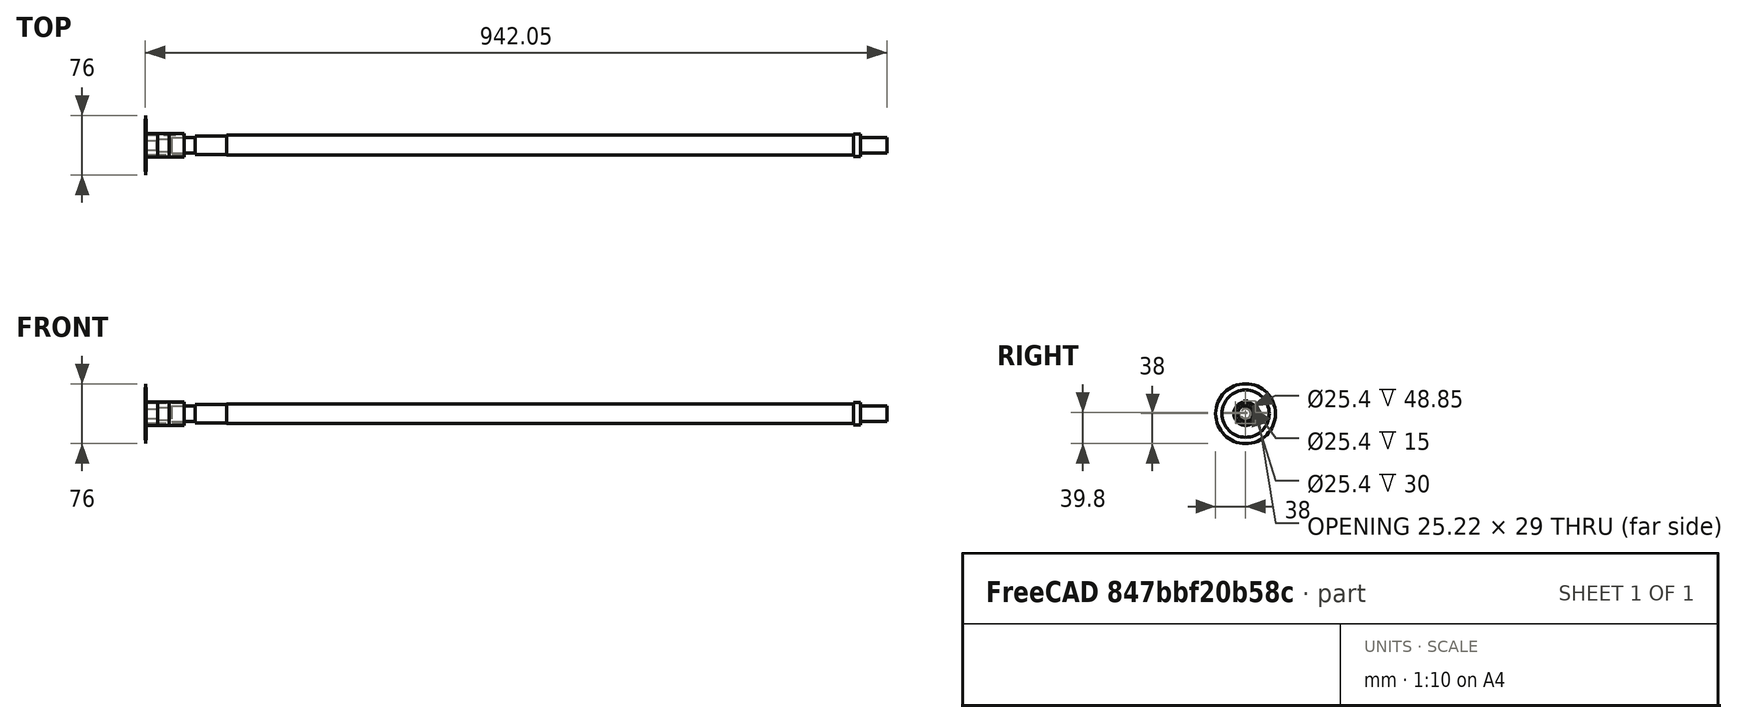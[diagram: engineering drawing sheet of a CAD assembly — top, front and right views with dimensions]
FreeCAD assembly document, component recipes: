
FREECAD ASSEMBLY — COMPONENT RECIPES ("cutting_roll")

This assembly document has 5 components, labeled P0..P4 below (a component is one placed body or linked part). 5 of them carry a construction recipe — the FreeCAD feature program that regenerates the part from scratch, quoted from this document or its linked companion documents; the rest are supplied as boundary geometry only. No exploded tour is included for this assembly.
COMPONENT P0 — recipe-attached ("spacer_49mm", modeled in this document).
Construction recipe (the document's own serialized feature program — sketch geometry with constraints, then the solid features built on it; lengths are millimeters unless a unit is written):

FEATURE [Sketcher::SketchObject] Sketch
  FullyConstrained = true
  MapMode = 5
  Placement = pos=(0,0,0) rot=(0.57735,0.57735,0.57735;2.0944rad)
  Support = -> [YZ_Plane]
  sketch-geometry (2):
    g0: Circle CenterX=0 CenterY=0 CenterZ=0 NormalX=0 NormalY=0 NormalZ=1 AngleXU=0 Radius=14.85
    g1: Circle CenterX=0 CenterY=0 CenterZ=0 NormalX=0 NormalY=0 NormalZ=1 AngleXU=0 Radius=12.7
  constraints (4):
    c: Coincident(g0,g-1)
    c: Diameter(g0) = 29.7  'outer_d'
    c: Coincident(g1,g0)
    c: Diameter(g1) = 25.4  'inner_d'
FEATURE [PartDesign::Pad] Pad  label="spacer_49_pad"
  Direction = (1,-2e-16,3e-16)
  Length = 48.85
  Length2 = 10
  Placement = pos=(0,0,0) rot=(0.57735,0.57735,0.57735;2.0944rad)
  Profile = -> Sketch
  ReferenceAxis = -> Sketch [N_Axis]
  Type = 0
FEATURE [PartDesign::CoordinateSystem] front
  AttacherType = Attacher::AttachEngine3D
  MapMode = 5
  Support = -> [XY_Plane]
FEATURE [PartDesign::CoordinateSystem] back
  AttacherType = Attacher::AttachEngine3D
  AttachmentOffset = pos=(48.85,0,0) rot=(0,0,1;0rad)
  MapMode = 5
  Placement = pos=(48.85,0,0) rot=(0,0,1;0rad)
  Support = -> [XY_Plane]
  expr: .AttachmentOffset.Base.x = Pad.Length
FEATURE [PartDesign::Body] Body  label="spacer_49mm"
  Group = -> [Sketch,Pad,front,back]
  Origin = -> Origin
  Tip = -> Pad
COMPONENT P1 — recipe-attached ("cutting_disk", modeled in this document).
Construction recipe (the document's own serialized feature program — sketch geometry with constraints, then the solid features built on it; lengths are millimeters unless a unit is written):

FEATURE [Sketcher::SketchObject] Sketch001  label="disk_sketch"
  FullyConstrained = true
  MapMode = 5
  Placement = pos=(0,0,0) rot=(1,0,0;1.5708rad)
  Support = -> [XZ_Plane001]
  sketch-geometry (4):
    g0: LineSegment StartX=0 StartY=38 StartZ=0 EndX=0.55 EndY=30 EndZ=0
    g1: LineSegment StartX=0.55 StartY=30 StartZ=0 EndX=0.55 EndY=0 EndZ=0
    g2: LineSegment StartX=0.55 StartY=0 StartZ=0 EndX=0 EndY=0 EndZ=0
    g3: LineSegment StartX=0 StartY=0 StartZ=0 EndX=0 EndY=38 EndZ=0
  constraints (11):
    c: PointOnObject(g0,g-2)
    c: Coincident(g1,g0)
    c: Vertical(g1)
    c: Coincident(g2,g1)
    c: Horizontal(g2)
    c: Coincident(g3,g2)
    c: Coincident(g3,g0)
    c: Coincident(g2,g-1)
    c: Distance(g3) = 38  'r'
    c: Distance(g2) = 0.55  'thickness_x2'
    c: Distance(g1) = 30
FEATURE [PartDesign::Revolution] Revolution
  Angle = 360
  Axis = (1,0,0)
  Base = (0,0,0)
  Placement = pos=(0,0,0) rot=(1,0,0;1.5708rad)
  Profile = -> Sketch001
  ReferenceAxis = -> Sketch001 [H_Axis]
FEATURE [Sketcher::SketchObject] Sketch002
  FullyConstrained = true
  MapMode = 5
  Placement = pos=(0,0,0) rot=(0.57735,0.57735,0.57735;2.0944rad)
  Support = -> [YZ_Plane001]
  sketch-geometry (4):
    g0: LineSegment StartX=3 StartY=12.3406 StartZ=0 EndX=3 EndY=16.3 EndZ=0
    g1: LineSegment StartX=3 StartY=16.3 StartZ=0 EndX=0 EndY=16.3 EndZ=0
    g2: LineSegment StartX=0 StartY=16.3 StartZ=0 EndX=0 EndY=-12.7 EndZ=0
    g3: ArcOfCircle CenterX=0 CenterY=0 CenterZ=0 NormalX=0 NormalY=0 NormalZ=1 AngleXU=0 Radius=12.7 StartAngle=4.71239 EndAngle=7.61551
  constraints (12):
    c: Vertical(g0)
    c: Coincident(g0,g1)
    c: PointOnObject(g1,g-2)
    c: Horizontal(g1)
    c: Coincident(g1,g2)
    c: PointOnObject(g2,g-2)
    c: Coincident(g3,g-1)
    c: Coincident(g3,g2)
    c: Coincident(g3,g0)
    c: Diameter(g3) = 25.4
    c: Distance(g1) = 3
    c: Distance(g2) = 29
FEATURE [PartDesign::Mirrored] Mirrored
  BaseFeature = -> Revolution
  MirrorPlane = -> Sketch001 [V_Axis]
  Originals = -> [Revolution]
  Placement = pos=(0,0,0) rot=(1,0,0;1.5708rad)
FEATURE [PartDesign::Pocket] Pocket
  BaseFeature = -> Mirrored
  Direction = (-1,2e-16,-3e-16)
  Length = 5
  Length2 = 5
  Midplane = true
  Placement = pos=(0,0,0) rot=(1,0,0;1.5708rad)
  Profile = -> Sketch002
  ReferenceAxis = -> Sketch002 [N_Axis]
  Type = 1
FEATURE [PartDesign::Mirrored] Mirrored001
  BaseFeature = -> Pocket
  MirrorPlane = -> Sketch002 [V_Axis]
  Originals = -> [Pocket]
  Placement = pos=(0,0,0) rot=(1,0,0;1.5708rad)
FEATURE [PartDesign::CoordinateSystem] Local_CS002  label="disk_end"
  AttacherType = Attacher::AttachEngine3D
  AttachmentOffset = pos=(0.55,0,0) rot=(0,0,1;0rad)
  MapMode = 5
  Placement = pos=(0.55,0,0) rot=(0,0,1;0rad)
  Support = -> [XY_Plane001]
  expr: .AttachmentOffset.Base.x = Sketch001.Constraints.thickness_x2
FEATURE [PartDesign::CoordinateSystem] Local_CS003  label="disk_begin"
  AttacherType = Attacher::AttachEngine3D
  AttachmentOffset = pos=(-0.55,0,0) rot=(0,0,1;0rad)
  MapMode = 5
  Placement = pos=(-0.55,0,0) rot=(0,0,1;0rad)
  Support = -> [XY_Plane001]
  expr: .AttachmentOffset.Base.x = -Sketch001.Constraints.thickness_x2
FEATURE [PartDesign::CoordinateSystem] Local_CS006  label="disk_middle"
  AttacherType = Attacher::AttachEngine3D
  MapMode = 5
  Support = -> [XY_Plane001]
FEATURE [PartDesign::Body] Body001  label="cutting_disk"
  Group = -> [Sketch001,Revolution,Sketch002,Mirrored,Pocket,Mirrored001,Local_CS002,Local_CS003,Local_CS006]
  Origin = -> Origin001
  Tip = -> Mirrored001
COMPONENT P2 — recipe-attached ("spacer_15mm", modeled in this document).
Construction recipe (the document's own serialized feature program — sketch geometry with constraints, then the solid features built on it; lengths are millimeters unless a unit is written):

FEATURE [Sketcher::SketchObject] Sketch003
  FullyConstrained = true
  MapMode = 5
  Placement = pos=(0,0,0) rot=(0.57735,0.57735,0.57735;2.0944rad)
  Support = -> [YZ_Plane004]
  sketch-geometry (2):
    g0: Circle CenterX=0 CenterY=0 CenterZ=0 NormalX=0 NormalY=0 NormalZ=1 AngleXU=0 Radius=14.85
    g1: Circle CenterX=0 CenterY=0 CenterZ=0 NormalX=0 NormalY=0 NormalZ=1 AngleXU=0 Radius=12.7
  constraints (4):
    c: Coincident(g0,g-1)
    c: Diameter(g0) = 29.7
    c: Coincident(g1,g0)
    c: Diameter(g1) = 25.4
FEATURE [PartDesign::Pad] Pad001
  Direction = (1,-2e-16,3e-16)
  Length = 15
  Length2 = 10
  Placement = pos=(0,0,0) rot=(0.57735,0.57735,0.57735;2.0944rad)
  Profile = -> Sketch003
  ReferenceAxis = -> Sketch003 [N_Axis]
  Type = 0
FEATURE [PartDesign::CoordinateSystem] back001
  AttacherType = Attacher::AttachEngine3D
  AttachmentOffset = pos=(15,0,0) rot=(0,0,1;0rad)
  MapMode = 5
  Placement = pos=(15,0,0) rot=(0,0,1;0rad)
  Support = -> [XY_Plane004]
  expr: .AttachmentOffset.Base.x = Pad001.Length
FEATURE [PartDesign::CoordinateSystem] front001
  AttacherType = Attacher::AttachEngine3D
  MapMode = 5
  Support = -> [XY_Plane004]
FEATURE [PartDesign::Body] Body002  label="spacer_15mm"
  Group = -> [Sketch003,Pad001,front001,back001]
  Origin = -> Origin004
  Tip = -> Pad001
COMPONENT P3 — recipe-attached ("spacer_30mm", modeled in this document).
Construction recipe (the document's own serialized feature program — sketch geometry with constraints, then the solid features built on it; lengths are millimeters unless a unit is written):

FEATURE [Sketcher::SketchObject] Sketch004
  FullyConstrained = true
  MapMode = 5
  Placement = pos=(0,0,0) rot=(0.57735,0.57735,0.57735;2.0944rad)
  Support = -> [YZ_Plane005]
  sketch-geometry (2):
    g0: Circle CenterX=0 CenterY=0 CenterZ=0 NormalX=0 NormalY=0 NormalZ=1 AngleXU=0 Radius=14.85
    g1: Circle CenterX=0 CenterY=0 CenterZ=0 NormalX=0 NormalY=0 NormalZ=1 AngleXU=0 Radius=12.7
  constraints (4):
    c: Coincident(g0,g-1)
    c: Diameter(g0) = 29.7
    c: Coincident(g1,g0)
    c: Diameter(g1) = 25.4
FEATURE [PartDesign::Pad] Pad002
  Direction = (1,-2e-16,3e-16)
  Length = 30
  Length2 = 10
  Placement = pos=(0,0,0) rot=(0.57735,0.57735,0.57735;2.0944rad)
  Profile = -> Sketch004
  ReferenceAxis = -> Sketch004 [N_Axis]
  Type = 0
FEATURE [PartDesign::CoordinateSystem] back002
  AttacherType = Attacher::AttachEngine3D
  AttachmentOffset = pos=(30,0,0) rot=(0,0,1;0rad)
  MapMode = 5
  Placement = pos=(30,0,0) rot=(0,0,1;0rad)
  Support = -> [XY_Plane005]
  expr: .AttachmentOffset.Base.x = Pad002.Length
FEATURE [PartDesign::CoordinateSystem] front002
  AttacherType = Attacher::AttachEngine3D
  MapMode = 5
  Support = -> [XY_Plane005]
FEATURE [PartDesign::Body] Body003  label="spacer_30mm"
  Group = -> [Sketch004,Pad002,front002,back002]
  Origin = -> Origin005
  Tip = -> Pad002
COMPONENT P4 — recipe-attached ("axis", modeled in this document).
Construction recipe (the document's own serialized feature program — sketch geometry with constraints, then the solid features built on it; lengths are millimeters unless a unit is written):

FEATURE [PartDesign::CoordinateSystem] LCS_0
  AttacherType = Attacher::AttachEngine3D
  MapMode = 2
  Support = -> [X_Axis006]
FEATURE [Sketcher::SketchObject] Sketch006
  FullyConstrained = true
  MapMode = 5
  Placement = pos=(0,0,0) rot=(1,0,0;1.5708rad)
  Support = -> [XZ_Plane006]
  sketch-geometry (18):
    g0: LineSegment StartX=0 StartY=0 StartZ=0 EndX=0 EndY=6 EndZ=0
    g1: LineSegment StartX=0 StartY=6 StartZ=0 EndX=14 EndY=6 EndZ=0
    g2: LineSegment StartX=16 StartY=6.25 StartZ=0 EndX=16 EndY=8 EndZ=0
    g3: LineSegment StartX=16 StartY=8 StartZ=0 EndX=33 EndY=8 EndZ=0
    g4: LineSegment StartX=33 StartY=8 StartZ=0 EndX=33 EndY=10 EndZ=0
    g5: LineSegment StartX=33 StartY=10 StartZ=0 EndX=63 EndY=10 EndZ=0
    g6: LineSegment StartX=63 StartY=10 StartZ=0 EndX=63 EndY=12 EndZ=0
    g7: LineSegment StartX=63 StartY=12 StartZ=0 EndX=103 EndY=12 EndZ=0
    g8: LineSegment StartX=103 StartY=12 StartZ=0 EndX=103 EndY=12.65 EndZ=0
    g9: LineSegment StartX=941.5 StartY=0 StartZ=0 EndX=0 EndY=0 EndZ=0
    g10: LineSegment StartX=899 StartY=12.65 StartZ=0 EndX=899 EndY=14.25 EndZ=0
    g11: LineSegment StartX=899 StartY=14.25 StartZ=0 EndX=907.8 EndY=14.25 EndZ=0
    g12: LineSegment StartX=907.8 StartY=14.25 StartZ=0 EndX=907.8 EndY=10 EndZ=0
    g13: LineSegment StartX=907.8 StartY=10 StartZ=0 EndX=941.5 EndY=10 EndZ=0
    g14: LineSegment StartX=941.5 StartY=10 StartZ=0 EndX=941.5 EndY=0 EndZ=0
    g15: LineSegment StartX=14 StartY=6 StartZ=0 EndX=16 EndY=6.25 EndZ=0
    g16: LineSegment StartX=103 StartY=12.65 StartZ=0 EndX=501 EndY=12.65 EndZ=0
    g17: LineSegment StartX=501 StartY=12.65 StartZ=0 EndX=899 EndY=12.65 EndZ=0
  constraints (58):
    c: Coincident(g-1,g0)
    c: PointOnObject(g0,g-2)
    c: Coincident(g0,g1)
    c: Horizontal(g1)
    c: Vertical(g2)
    c: Coincident(g2,g3)
    c: Horizontal(g3)
    c: Coincident(g3,g4)
    c: Vertical(g4)
    c: Coincident(g4,g5)
    c: Horizontal(g5)
    c: Coincident(g5,g6)
    c: Vertical(g6)
    c: Coincident(g6,g7)
    c: Horizontal(g7)
    c: Coincident(g7,g8)
    c: Vertical(g8)
    c: Coincident(g8,g16)
    c: PointOnObject(g9,g-1)
    c: Coincident(g9,g0)
    c: DistanceY(g0) = 6
    c: DistanceY(g2) = 8
    c: DistanceY(g4) = 10
    c: DistanceY(g6) = 12
    c: DistanceY(g8) = 12.65
    c: Distance(g3) = 17
    c: Distance(g5) = 30
    c: Distance(g7) = 40  'thread2_length'
    c: Coincident(g17,g10)
    c: Vertical(g10)
    c: Coincident(g10,g11)
    c: Horizontal(g11)
    c: Coincident(g11,g12)
    c: Vertical(g12)
    c: Coincident(g12,g13)
    c: Horizontal(g13)
    c: Coincident(g13,g14)
    c: Coincident(g14,g9)
    c: Vertical(g14)
    c: Distance(g11) = 8.8
    c: Distance(g13) = 33.7
    c: DistanceY(g10) = 14.25
    c: DistanceY(g12) = 10
    c: DistanceX(g15,g2) = 2
    c: DistanceY(g15) = 6.25
    c: DistanceX(g2) = 16
    c: Coincident(g1,g15)
    c: Coincident(g2,g15)
    c: DistanceX(g8) = 103  'roll_begin'
    c: DistanceX(g17) = 899  'roll_end'
    c: DistanceX(g6) = 63  'left_20mm_end'
    c: DistanceX(g12) = 907.8  'right_20mm_end'
    c: Coincident(g16,g17)
    c: Horizontal(g16)
    c: Horizontal(g17)
    c: Distance(g16,g17) = 796
    c: Equal(g16,g17)
    c: DistanceX(g16) = 501  'roll_middle'
FEATURE [PartDesign::Revolution] Revolution001
  Angle = 360
  Axis = (1,0,0)
  Base = (0,0,0)
  Placement = pos=(0,0,0) rot=(1,0,0;1.5708rad)
  Profile = -> Sketch006
  ReferenceAxis = -> Sketch006 [H_Axis]
FEATURE [PartDesign::CoordinateSystem] Local_CS  label="roll_begin"
  AttacherType = Attacher::AttachEngine3D
  AttachmentOffset = pos=(103,0,0) rot=(0,0,1;0rad)
  MapMode = 5
  Placement = pos=(103,0,0) rot=(0,0,1;0rad)
  Support = -> [XY_Plane006]
  expr: .AttachmentOffset.Base.x = Sketch006.Constraints.roll_begin
FEATURE [PartDesign::CoordinateSystem] Local_CS001  label="roll_end"
  AttacherType = Attacher::AttachEngine3D
  AttachmentOffset = pos=(899,0,0) rot=(0,0,1;0rad)
  MapMode = 5
  Placement = pos=(899,0,0) rot=(0,0,1;0rad)
  Support = -> [XY_Plane006]
  expr: .AttachmentOffset.Base.x = Sketch006.Constraints.roll_end
FEATURE [Sketcher::SketchObject] Sketch007
  AttachmentOffset = pos=(-1.75,0,0) rot=(0,0,1;0rad)
  FullyConstrained = true
  MapMode = 5
  Placement = pos=(-1.75,0,0) rot=(0,0,1;0rad)
  Support = -> [XY_Plane006]
  expr: .AttachmentOffset.Base.x = -1.75
  sketch-geometry (6):
    g0: LineSegment StartX=-0.1095 StartY=5.053 StartZ=0 EndX=0 EndY=5.053 EndZ=0
    g1: LineSegment StartX=0 StartY=5.053 StartZ=0 EndX=0.1095 EndY=5.053 EndZ=0
    g2: LineSegment StartX=0.1095 StartY=5.053 StartZ=0 EndX=0.656251 EndY=6 EndZ=0
    g3: LineSegment StartX=0.656251 StartY=6 StartZ=0 EndX=0 EndY=6 EndZ=0
    g4: LineSegment StartX=0 StartY=6 StartZ=0 EndX=-0.656251 EndY=6 EndZ=0
    g5: LineSegment StartX=-0.656251 StartY=6 StartZ=0 EndX=-0.1095 EndY=5.053 EndZ=0
  constraints (18):
    c: PointOnObject(g0,g-2)
    c: Horizontal(g0)
    c: Coincident(g0,g1)
    c: Horizontal(g1)
    c: Coincident(g1,g2)
    c: Coincident(g2,g3)
    c: PointOnObject(g3,g-2)
    c: Horizontal(g3)
    c: Coincident(g3,g4)
    c: Horizontal(g4)
    c: Coincident(g4,g5)
    c: Coincident(g5,g0)
    c: Equal(g0,g1)
    c: Equal(g4,g3)
    c: DistanceY(g3) = 6
    c: DistanceY(g0) = 5.053
    c: DistanceX(g0,g1) = 0.219
    c: Angle(g-2,g2) = 2.61799
FEATURE [Sketcher::SketchObject] Sketch008
  AttachmentOffset = pos=(61.813,0,0) rot=(0,0,1;0rad)
  FullyConstrained = true
  MapMode = 5
  Placement = pos=(61.813,0,0) rot=(0,0,1;0rad)
  Support = -> [XY_Plane006]
  expr: .AttachmentOffset.Base.x = Sketch006.Constraints.roll_begin - Sketch006.Constraints.thread2_length - (.Constraints.root + sin(30) * (.Constraints.major_r - .Constraints.minor_r))
  sketch-geometry (6):
    g0: LineSegment StartX=0 StartY=10.376 StartZ=0 EndX=0.1875 EndY=10.376 EndZ=0
    g1: LineSegment StartX=0.1875 StartY=10.376 StartZ=0 EndX=1.12512 EndY=12 EndZ=0
    g2: LineSegment StartX=1.12512 StartY=12 StartZ=0 EndX=0 EndY=12 EndZ=0
    g3: LineSegment StartX=0 StartY=12 StartZ=0 EndX=-1.12512 EndY=12 EndZ=0
    g4: LineSegment StartX=-1.12512 StartY=12 StartZ=0 EndX=-0.1875 EndY=10.376 EndZ=0
    g5: LineSegment StartX=-0.1875 StartY=10.376 StartZ=0 EndX=0 EndY=10.376 EndZ=0
  constraints (19):
    c: PointOnObject(g0,g-2)
    c: Horizontal(g0)
    c: Coincident(g0,g1)
    c: Coincident(g1,g2)
    c: PointOnObject(g2,g-2)
    c: Horizontal(g2)
    c: Coincident(g2,g3)
    c: Horizontal(g3)
    c: Coincident(g3,g4)
    c: Coincident(g4,g5)
    c: Coincident(g5,g0)
    c: Horizontal(g5)
    c: Equal(g5,g0)
    c: Equal(g3,g2)
    c: Angle(g-2,g1) = 2.61799
    c: DistanceY(g2) = 12  'major_r'
    c: DistanceY(g0) = 10.376  'minor_r'
    c: DistanceX(g4,g0) = 0.375  'root'
    c: Distance(g1,g3) = 2.25023  'top_distance'
FEATURE [PartDesign::CoordinateSystem] Local_CS004  label="left_20mm"
  AttacherType = Attacher::AttachEngine3D
  AttachmentOffset = pos=(63,0,0) rot=(0.57735,-0.57735,-0.57735;2.0944rad)
  MapMode = 5
  Placement = pos=(63,0,0) rot=(0.57735,-0.57735,-0.57735;2.0944rad)
  Support = -> [XY_Plane006]
  expr: .AttachmentOffset.Base.x = Sketch006.Constraints.left_20mm_end
FEATURE [PartDesign::CoordinateSystem] Local_CS005  label="right_20mm"
  AttacherType = Attacher::AttachEngine3D
  AttachmentOffset = pos=(907.8,0,0) rot=(0.57735,0.57735,0.57735;2.0944rad)
  MapMode = 5
  Placement = pos=(907.8,0,0) rot=(0.57735,0.57735,0.57735;2.0944rad)
  Support = -> [XY_Plane006]
  expr: .AttachmentOffset.Base.x = Sketch006.Constraints.right_20mm_end
FEATURE [PartDesign::CoordinateSystem] roll_middle
  AttacherType = Attacher::AttachEngine3D
  AttachmentOffset = pos=(501,0,0) rot=(0,0,1;0rad)
  MapMode = 5
  Placement = pos=(501,0,0) rot=(0,0,1;0rad)
  Support = -> [XY_Plane006]
  expr: .AttachmentOffset.Base.x = Sketch006.Constraints.roll_middle
FEATURE [PartDesign::Body] axis
  Group = -> [LCS_0,Sketch006,Revolution001,Local_CS,Local_CS001,Sketch007,Sketch008,Local_CS004,Local_CS005,roll_middle]
  Origin = -> Origin006
  Tip = -> Revolution001
PROVENANCE & LICENSES
A FreeCAD (.FCStd) document from a public repository crawl; recipes are the document's own serialized feature recipes (and, for linked parts, companion documents' recipes).
License: as declared in the source repository (recorded in the dataset sidecar).
